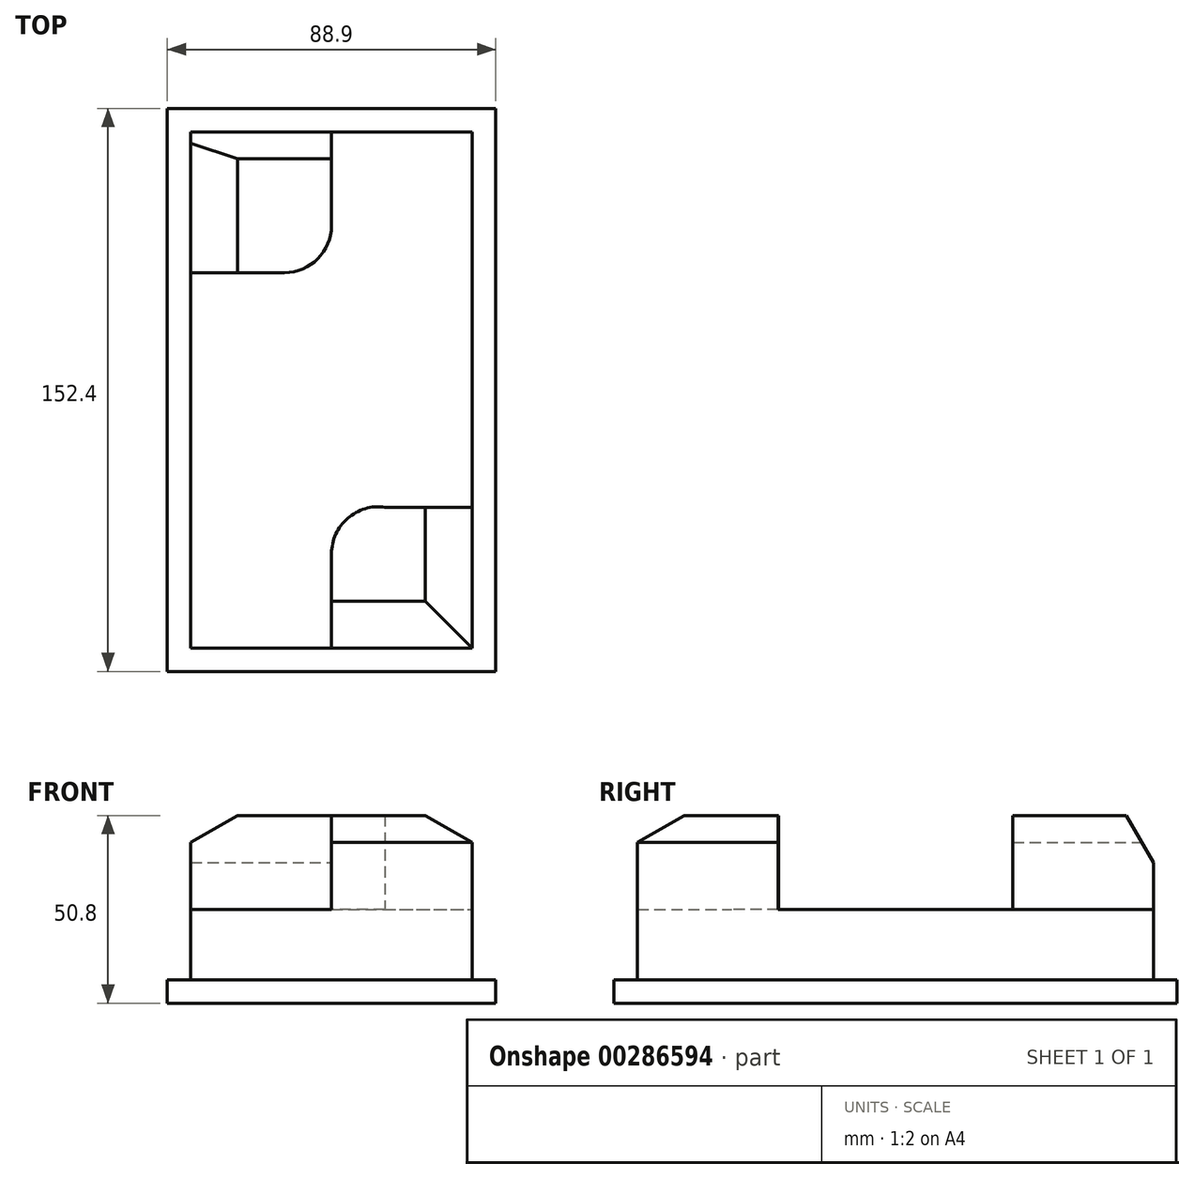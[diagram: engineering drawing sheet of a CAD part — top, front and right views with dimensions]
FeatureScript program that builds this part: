
annotation { "Feature Type Name" : "Feature", "Feature Type Description" : "" }
export const myFeature = defineFeature(function(context is Context, id is Id, definition is map)
    precondition{}
    {
        {
            var Q0;
            Q0=qCreatedBy(makeId("Top.planeOp"),FACE);
            var sketch = newSketch(context, id + "F0", { "sketchPlane" : qUnion([Q0])});
            skLineSegment(sketch, "E0.bottom", {"start": v(-75.63, 87.53) * mm, "end": v(13.27, 87.53) * mm});
            skLineSegment(sketch, "E0.top", {"start": v(-75.63, -64.87) * mm, "end": v(13.27, -64.87) * mm});
            skLineSegment(sketch, "E0.left", {"start": v(-75.63, 87.53) * mm, "end": v(-75.63, -64.87) * mm});
            skLineSegment(sketch, "E0.right", {"start": v(13.27, 87.53) * mm, "end": v(13.27, -64.87) * mm});
            skLineSegment(sketch, "E1.bottom", {"start": v(-69.28, 81.18) * mm, "end": v(6.92, 81.18) * mm});
            skLineSegment(sketch, "E1.top", {"start": v(-69.28, -58.52) * mm, "end": v(6.92, -58.52) * mm});
            skLineSegment(sketch, "E1.left", {"start": v(-69.28, 81.18) * mm, "end": v(-69.28, -58.52) * mm});
            skLineSegment(sketch, "E1.right", {"start": v(6.92, 81.18) * mm, "end": v(6.92, -58.52) * mm});
            skLineSegment(sketch, "E2", {"start": v(-31.18, 81.18) * mm, "end": v(-31.18, 55.78) * mm});
            skLineSegment(sketch, "E3", {"start": v(-43.88, 43.08) * mm, "end": v(-69.28, 43.08) * mm});
            skLineSegment(sketch, "E4", {"start": v(-31.18, -58.52) * mm, "end": v(-31.18, -33) * mm});
            skLineSegment(sketch, "E5", {"start": v(-16.74, -20.42) * mm, "end": v(6.92, -20.42) * mm});
            skArc(sketch, "E6", {"start": v(-16.74, -20.42) * mm, "mid": v(-26.82, -23.43) * mm, "end": v(-31.18, -33) * mm});
            skArc(sketch, "E7", {"start": v(-43.88, 43.08) * mm, "mid": v(-34.9, 46.8) * mm, "end": v(-31.18, 55.78) * mm});
            skSolve(sketch);
        }
        {
            var Q0;
            Q0=makeQuery(id+"F0.imprint","IMPRINT",FACE,{"disambiguationData":[TD([[makeQuery(id+"F0.imprint","IMPRINT",EDGE,{"derivedFrom":sQuery(id+"F0.wireOp",EDGE,"E0.bottom")}),-1.0]])]});
            extrude(context, id + "F1", {"entities" : qUnion([Q0]), "depth" : 6.35 * mm});
        }
        {
            var Q0;
            {var subQ9=sQuery(id+"F0.wireOp",EDGE,"E2");Q0=makeQuery(id+"F0.imprint","IMPRINT",FACE,{"disambiguationData":[TD([[makeQuery(id+"F0.imprint","IMPRINT",EDGE,{"derivedFrom":subQ9}),1.0]])]});}
            extrude(context, id + "F2", {"entities" : qUnion([Q0]), "operationType" : NewBodyOperationType.ADD, "depth" : 25.4 * mm});
        }
        {
            var Q0;
            {var subQ0=sQuery(id+"F0.wireOp",EDGE,"E2");Q0=makeQuery(id+"F0.imprint","IMPRINT",FACE,{"disambiguationData":[TD([[makeQuery(id+"F0.imprint","IMPRINT",EDGE,{"derivedFrom":subQ0}),-1.0]])]});}
            var Q1;
            {var subQ1=sQuery(id+"F0.wireOp",EDGE,"E4");Q1=makeQuery(id+"F0.imprint","IMPRINT",FACE,{"disambiguationData":[TD([[makeQuery(id+"F0.imprint","IMPRINT",EDGE,{"derivedFrom":subQ1}),-1.0]])]});}
            extrude(context, id + "F3", {"entities" : qUnion([Q0, Q1]), "operationType" : NewBodyOperationType.ADD, "depth" : 50.8 * mm});
        }
        {
            var Q0;
            Q0=makeQuery(id+"F3.opExtrude","CAP_EDGE",EDGE,{"disambiguationData":[OSD([sQuery(id+"F0.wireOp",EDGE,"E1.top")])],"isStart":false});
            var Q1;
            Q1=makeQuery(id+"F3.opExtrude","CAP_EDGE",EDGE,{"disambiguationData":[OSD([sQuery(id+"F0.wireOp",EDGE,"E1.right")])],"isStart":false});
            var Q2;
            Q2=makeQuery(id+"F3.opExtrude","CAP_EDGE",EDGE,{"disambiguationData":[OSD([sQuery(id+"F0.wireOp",EDGE,"E1.bottom")])],"isStart":false});
            var Q3;
            Q3=makeQuery(id+"F3.opExtrude","CAP_EDGE",EDGE,{"disambiguationData":[OSD([sQuery(id+"F0.wireOp",EDGE,"E1.left")])],"isStart":false});
            chamfer(context, id + "F4", {"entities" : qUnion([Q0, Q1, Q2, Q3]), "chamferType" : ChamferType.OFFSET_ANGLE, "width" : 12.7 * mm, "oppositeDirection" : false, "angle" : 30 * degree, "tangentPropagation" : true});
        }
    });
